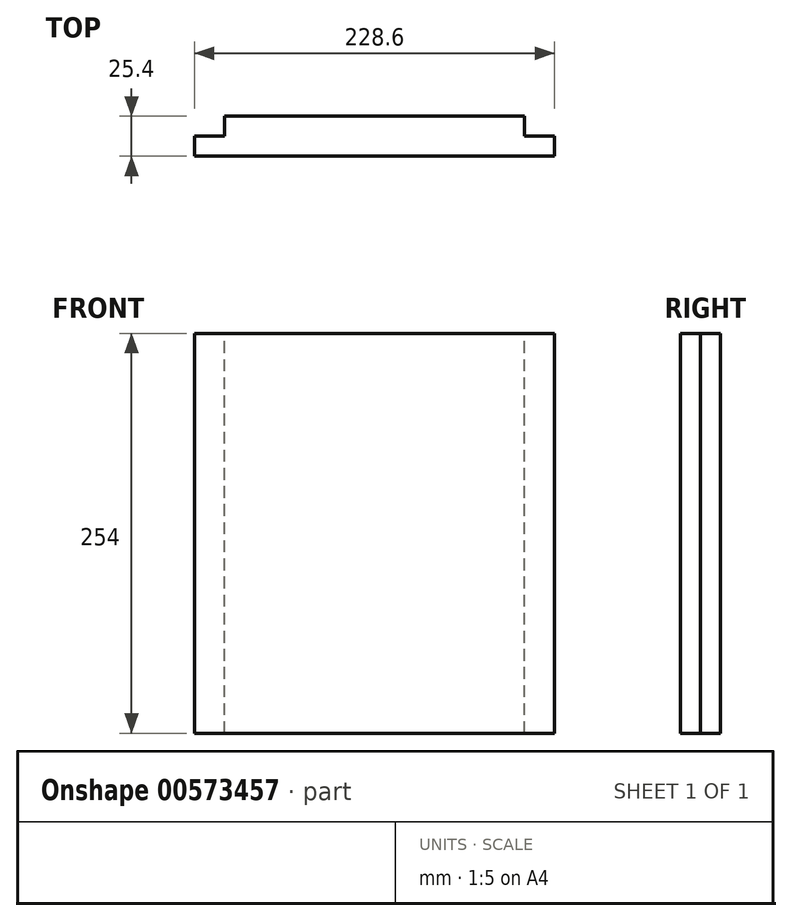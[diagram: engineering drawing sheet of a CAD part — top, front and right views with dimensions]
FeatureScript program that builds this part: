
annotation { "Feature Type Name" : "Feature", "Feature Type Description" : "" }
export const myFeature = defineFeature(function(context is Context, id is Id, definition is map)
    precondition{}
    {
        {
            var Q0;
            Q0=qCreatedBy(makeId("Front.planeOp"),FACE);
            var sketch = newSketch(context, id + "F0", { "sketchPlane" : qUnion([Q0])});
            skLineSegment(sketch, "E0.bottom", {"start": v(-114.3, 127) * mm, "end": v(114.3, 127) * mm});
            skLineSegment(sketch, "E0.top", {"start": v(-114.3, -127) * mm, "end": v(114.3, -127) * mm});
            skLineSegment(sketch, "E0.left", {"start": v(-114.3, 127) * mm, "end": v(-114.3, -127) * mm});
            skLineSegment(sketch, "E0.right", {"start": v(114.3, 127) * mm, "end": v(114.3, -127) * mm});
            skPoint(sketch, "E0.middle", {"position": v(0, 0) * mm});
            skPoint(sketch, "E1.middle", {"position": v(0, -127) * mm});
            skSolve(sketch);
        }
        {
            var Q0;
            Q0=makeQuery(id+"F0.imprint","IMPRINT",FACE,{"disambiguationData":[TD([[makeQuery(id+"F0.imprint","IMPRINT",EDGE,{"derivedFrom":sQuery(id+"F0.wireOp",EDGE,"E0.bottom")}),-1.0]])]});
            var Q1;
            {var subQ1=sQuery(id+"F0.wireOp",EDGE,"E0.top");Q1=makeQuery(id+"F0.imprint","IMPRINT",FACE,{"disambiguationData":[TD([[makeQuery(id+"F0.imprint","IMPRINT",EDGE,{"derivedFrom":subQ1}),-1.0]])]});}
            var Q2;
            {var subQ0=sQuery(id+"F0.wireOp",EDGE,"E0.top");Q2=makeQuery(id+"F0.imprint","IMPRINT",FACE,{"disambiguationData":[TD([[makeQuery(id+"F0.imprint","IMPRINT",EDGE,{"derivedFrom":subQ0}),1.0]])]});}
            extrude(context, id + "F1", {"entities" : qUnion([Q0, Q1, Q2]), "depth" : 25.4 * mm, "offsetDistance" : 25.4 * mm});
        }
        {
            var Q0;
            Q0=makeQuery(id+"F1.opExtrude","SWEPT_FACE",FACE,{"disambiguationData":[OSD([sQuery(id+"F0.wireOp",EDGE,"E0.bottom")])]});
            var sketch = newSketch(context, id + "F2", { "sketchPlane" : qUnion([Q0])});
            skLineSegment(sketch, "E2.bottom", {"start": v(-114.3, 0) * mm, "end": v(-95.25, 0) * mm});
            skLineSegment(sketch, "E2.top", {"start": v(-114.3, -12.7) * mm, "end": v(-95.25, -12.7) * mm});
            skLineSegment(sketch, "E2.left", {"start": v(-114.3, 0) * mm, "end": v(-114.3, -12.7) * mm});
            skLineSegment(sketch, "E2.right", {"start": v(-95.25, 0) * mm, "end": v(-95.25, -12.7) * mm});
            skLineSegment(sketch, "E3.bottom", {"start": v(114.3, 0) * mm, "end": v(95.25, 0) * mm});
            skLineSegment(sketch, "E3.top", {"start": v(114.3, -12.7) * mm, "end": v(95.25, -12.7) * mm});
            skLineSegment(sketch, "E3.left", {"start": v(114.3, 0) * mm, "end": v(114.3, -12.7) * mm});
            skLineSegment(sketch, "E3.right", {"start": v(95.25, 0) * mm, "end": v(95.25, -12.7) * mm});
            skSolve(sketch);
        }
        {
            var Q0;
            Q0=makeQuery(id+"F2.imprint","IMPRINT",FACE,{"disambiguationData":[TD([[makeQuery(id+"F2.imprint","IMPRINT",EDGE,{"derivedFrom":sQuery(id+"F2.wireOp",EDGE,"E2.bottom")}),-1.0]])]});
            var Q1;
            Q1=makeQuery(id+"F2.imprint","IMPRINT",FACE,{"disambiguationData":[TD([[makeQuery(id+"F2.imprint","IMPRINT",EDGE,{"derivedFrom":sQuery(id+"F2.wireOp",EDGE,"E3.bottom")}),-1.0]])]});
            extrude(context, id + "F3", {"entities" : qUnion([Q0, Q1]), "operationType" : NewBodyOperationType.REMOVE, "oppositeDirection" : true, "depth" : 254 * mm, "offsetDistance" : 25.4 * mm});
        }
    });
